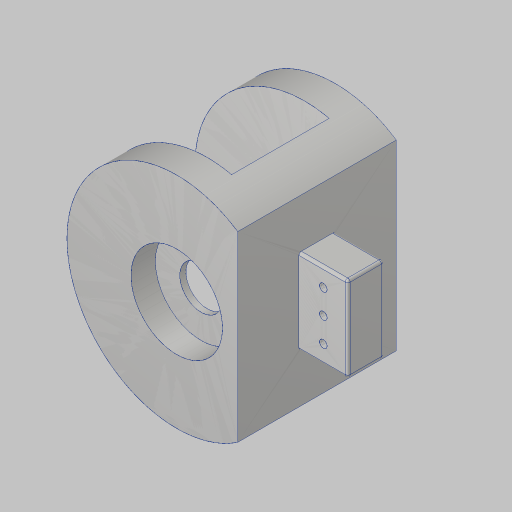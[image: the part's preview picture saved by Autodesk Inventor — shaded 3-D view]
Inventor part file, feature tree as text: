
AUTODESK INVENTOR PART (.ipt)
format: ipt  version: 2023.5 (Build 275446000, 446)  size: 256,000 bytes
history: native  units: in
note: dims shown in document units (in); Inventor stores cm internally (conversion verified against a paired STEP export)
features: sketch x6, extrude x5, projected_geometry x2, hole x1, fillet x1
ambient origin geometry x8: Origin, YZ Plane, XZ Plane, XY Plane, X Axis, Y Axis, Z Axis, Center Point
bodies: Solid1 (feature_tree)
feature tree (15):
  extrude  "Extrusion1"  Depth=4.5in
  extrude  "Extrusion2"  Depth=0.25in
  extrude  "Extrusion3"  Depth=0.8358in
  extrude  "Extrusion5"  Depth=3.25in TaperAngle=0.0deg
  extrude  "Extrusion6"  Depth=0.5in TaperAngle=0.0deg
  hole  "Hole2"  [1 undecoded]
  fillet  "Fillet1"  Radius=1.0in
  sketch  "Sketch1"  dims[d0=0.875in d2=4.5in]
  sketch  "Sketch3"  dims[d3=3.5in d4=0.25in]
  sketch  "Sketch4"  dims[d5=1.4142in d6=0.8358in]
  sketch  "Sketch7"  dims[d7=1.25in d8=3.25in d9=0.0in]
  sketch  "Sketch8"  dims[d10=1.875in d11=0.5in d12=0.0in]
  sketch  "Sketch9"  dims[d13=1.875in d14=0.5in d15=0.0in d34=1.0in d35=2.0in d36=0.125in d37=0.125in d38=0.005in d39=0.005in d40=1.0in d41=0.0in d42=0.5in d43=2.0in d44=0.0in d45=0.5in d46=0.5in d47=0.5in d48=0.156in d49=0.38in d50=0.385in d51=0.25in d52=0.5635in d53=1.0in d54=0.8108in d55=0.05in]
  projected_geometry  "Project Cut Edges1"
  projected_geometry  "Project Cut Edges4"
note: 1 required parameter value undecoded (feature->parameter linkage not recoverable at this tier; creation-order binding heuristic only, values carry confidence <= 0.55)
